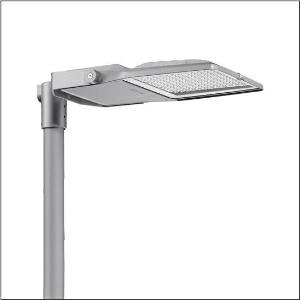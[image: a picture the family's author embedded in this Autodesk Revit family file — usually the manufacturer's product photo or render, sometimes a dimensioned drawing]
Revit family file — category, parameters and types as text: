
# Revit family: floodlight_fl_21_midi___pl43_5xa7785e2a3a_e2fe
name_source: partatom
category: Lighting Fixtures
units: mm (PartAtom-declared; Revit-internal decimal feet)

## family parameters
Cut with Voids When Loaded = No
Host = Face
Light Source = No
Part Type = Normal
Room Calculation Point = No
Round Connector Dimension = Use Diameter
Shared = No

## types (1)
- --- (1 x LED, 27640 lm, 212.4 W, 3000K)
    Apparent Load = 212 VA
    CIE Flux Codes = 27 78 99 100 100
    Color Rendering = 70
    Color Temperature = 3000K
    Default Elevation = 1800 mm
    Description = Floodlight FL 21 midi, floodlight, primary light control with lens, of PMMA, primary optical cover: protective disc, of toughened safety glass, transparent, light distribution: PL43, light emission: direct distribution, installation type: surface-mounted, LED, High Power LED, rated luminous flux: 27.640lm, luminous efficacy: 130lm/W, light colour: 730, colour temperature: 3000K, control gear: ECG Smart Interface, control: flexible luminous flux parameterisation, time-dependent luminous flux control, constant luminous flux control, overheat protection, pre-setting: logarithmic dimming characteristic, with terminal, 6-pole, mains connection: 220..240V, AC, 50/60Hz, start of lifetime: 212W, end of service life: 231W, reduction: 95W, luminaire housing, of diecast aluminium, powder-coated, Siteco® metallic grey (DB 702S), sealing non-destructively replaceable, please order mast flange separately, mast bracket, of steel, galvanised, powder-coated, Siteco® metallic grey (DB 702S), Smart Interface above, protection rating (complete): IP66, insulation class (complete): insulation class II (safety insulation), certification: CE, ENEC, VDE, protection symbol: D, impact resistance: IK08, permissible operating ambient temperature: -20..+40°C, permissible operating ambient temperature for outdoor applications: -40..+50°C, standard: DIN EN 12944, LABS conformity tested according to VDMA 24364:2018-05, packaging unit: 1 piece

Light Distribution: PL43
    Height = 76 mm
    Lamp = 1 x LED
    Lamp Light Flux = 27640 lm
    Lamp Power = 212.4 W
    Lamp count = 1
    Length = 657 mm
    Luminous efficacy = 130 lm/W
    Manufacturer = Siteco
    ModVariant = No
    Model = 5XA7785E2A3A
    Number of Poles = 1
    OnlyDefault = Yes
    Power Factor = 1
    Product Name = Floodlight FL 21 midi | PL43
    Product group = floodlight | pylon annexe
    ProductGroupID = 6200
    Protection Class = Protection class II
    Protection Degree = IP 66
    RLX_Detail_Level = 1
    RLX_Emergency_Light_Flux = 0 lm
    RLX_Emergency_Type = 0
    RLX_Emergency_Type_DB = No
    RlxData = <blob elided: 153741 chars, md5=9aceaba0>
    Socket = socket
    Standby Power = 0 W
    System Light Flux = 27640 lm
    System Power = 212 W
    Type Comments = factory setting: luminous flux: 100 % | dim-lin: 254 | 710 mA
    Type Image = l_1007123.jpg
    URL = http://relux.com
    VarID = @adj_148611
    Voltage = 0 V
    Weight = 0.00 kg
    Width = 442 mm

## geometry (parser evidence)
native form markers: Blend x4, Sweep x16
no freeform markers — native parametric forms only
